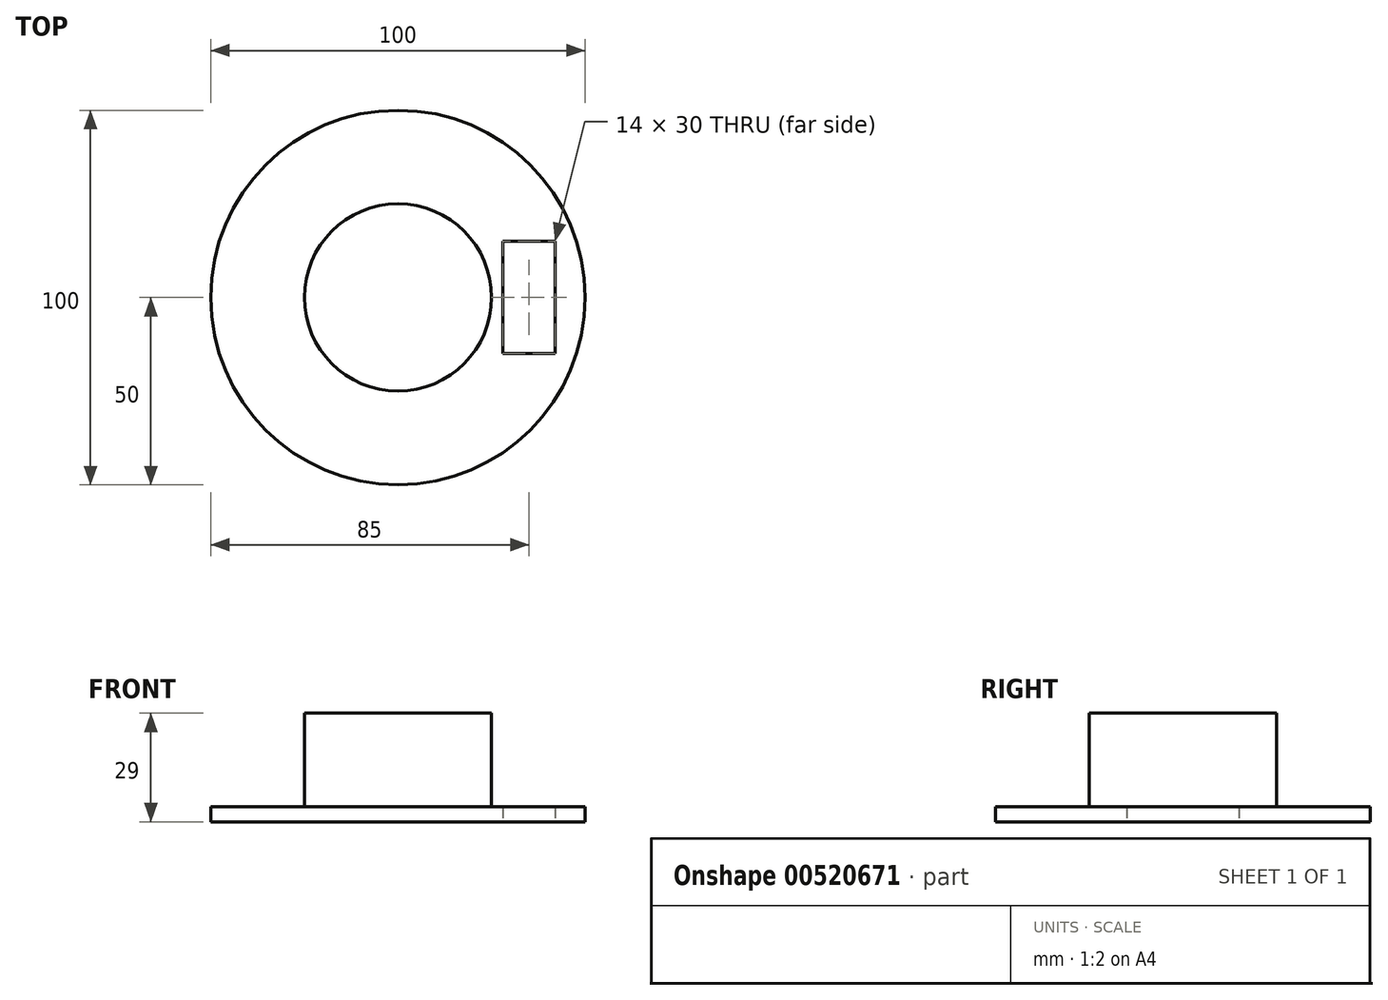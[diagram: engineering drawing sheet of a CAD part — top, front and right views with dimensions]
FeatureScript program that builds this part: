
annotation { "Feature Type Name" : "Feature", "Feature Type Description" : "" }
export const myFeature = defineFeature(function(context is Context, id is Id, definition is map)
    precondition{}
    {
        {
            var Q0;
            Q0=qCreatedBy(makeId("Top.planeOp"),FACE);
            var sketch = newSketch(context, id + "F0", { "sketchPlane" : qUnion([Q0])});
            skCircle(sketch, "E0", {"center": v(0, 0) * mm, "radius": 50 * mm});
            skSolve(sketch);
        }
        {
            var Q0;
            Q0 = qSketchRegion(id + "F0", true);
            extrude(context, id + "F1", {"entities" : qUnion([Q0]), "depth" : 4 * mm, "offsetDistance" : 25 * mm});
        }
        {
            var Q0;
            Q0=makeQuery(id+"F1.opExtrude","CAP_FACE",FACE,{"disambiguationData":[OSD([sQuery(id+"F0.wireOp",EDGE,"E0")])],"isStart":false});
            var sketch = newSketch(context, id + "F2", { "sketchPlane" : qUnion([Q0])});
            skCircle(sketch, "E1", {"center": v(0, 0) * mm, "radius": 25 * mm});
            skSolve(sketch);
        }
        {
            var Q0;
            Q0 = qSketchRegion(id + "F2", true);
            extrude(context, id + "F3", {"entities" : qUnion([Q0]), "operationType" : NewBodyOperationType.ADD, "depth" : 25 * mm, "offsetDistance" : 25 * mm});
        }
        {
            var Q0;
            Q0=makeQuery(id+"F1.opExtrude","CAP_FACE",FACE,{"disambiguationData":[OSD([sQuery(id+"F0.wireOp",EDGE,"E0")])],"isStart":true});
            var sketch = newSketch(context, id + "F4", { "sketchPlane" : qUnion([Q0])});
            skLineSegment(sketch, "E2.bottom", {"start": v(42, 15) * mm, "end": v(28, 15) * mm});
            skLineSegment(sketch, "E2.top", {"start": v(42, -15) * mm, "end": v(28, -15) * mm});
            skLineSegment(sketch, "E2.left", {"start": v(42, 15) * mm, "end": v(42, -15) * mm});
            skLineSegment(sketch, "E2.right", {"start": v(28, 15) * mm, "end": v(28, -15) * mm});
            skSolve(sketch);
        }
        {
            var Q0;
            Q0 = qSketchRegion(id + "F4", true);
            extrude(context, id + "F5", {"entities" : qUnion([Q0]), "operationType" : NewBodyOperationType.REMOVE, "oppositeDirection" : true, "depth" : 5 * mm, "offsetDistance" : 25 * mm});
        }
    });
